# Revit family: BDG_BossDesign_Tbls_ATOM_CircularTables1
name_source: partatom
category: Furniture
revit_build: Autodesk Revit 2016 (Build: 20150714_1515(x64)
units: mm (PartAtom-declared; Revit-internal decimal feet)

## family parameters
Always vertical = Yes
Cut with Voids When Loaded = No
OmniClass Number = 23.40.20.00
OmniClass Title = General Furniture and Specialties
Room Calculation Point = No
Shared = Yes
Work Plane-Based = No

## types (3) — shared parameters
Assembly Code = E2020200
AssetType = Movable
BIMObjectName = BDG_BossDesign_Tables_ATOM_CircularTables
Category = Pr_40_50_21 : Desks, tables and worktops
DurationUnit = year
ExpectedLife = 5
Finish = Black RAL 9005 or White RAL 9016 Painted Leg Finish

Standard Finishes - MFC, MF MDF, Compact Laminate, 
Premium Finishes - Oak & BAW Veneer, Fenix and Linoleum.
FrameMaterial = BDG_Generic_MFC_White
IfcExportAs = IfcFurnishingElementType
IfcExportType = TABLE
Keynote = Pr_40_50_21
ManufacturerURL = www.bossdesign.com
Material = Standard Finishes - MFC, MF MDF, Compact Laminate, 
Premium Finishes - Oak & BAW Veneer, Fenix and Linoleum.
NBSDescription = Tables
NBSReference = 45-35-86/327
Name = Tables_ATOM_CircularTables_BossDesign
NominalHeight = 735 mm
ProductInformation = www.bossdesign.com/product-list/atom-tables
Shape = Circular
TopMaterial = BDG_Generic_Wood_MFC
URL = www.bossdesign.com
Uniclass2015Code = Pr_40_50_21
Uniclass2015Title = Desks, tables and worktops
Uniclass2015Version = Products v1.10
Version = 1
WarrantyDurationLabor = 5
WarrantyDurationParts = 5
WarrantyDurationUnit = year
zero-valued in all types: NumberOfChairs, WorksurfaceArea

## per-type parameters (varying)
| type | FrameLength | Model | ModelNumber | NominalLength | NominalWidth | Size |
| 1200mm Circular Table | 800 mm  [stored 2.62467 ft] | BOSS_ATTC1200 | BOSS_ATTC1200 | 1200 mm | 1200 mm | 1200 x 1200 x 735mm |
| 1500mm Circular Table | 1000 mm  [stored 3.28084 ft] | BOSS_ATTC1500 | BOSS_ATTC1500 | 1500 mm  [stored 4.92126 ft] | 1500 mm  [stored 4.92126 ft] | 1500 x 1500 x 735mm |
| 1000mm Circular Table | 700 mm  [stored 2.29659 ft] | BOSS_ATTC1000 | BOSS_ATTC1000 | 1000 mm  [stored 3.28084 ft] | 1000 mm  [stored 3.28084 ft] | 1000 x 1000 x 735mm |

note: column(s) folded — value = type name in every type: Description, ModelReference

note: [stored X ft] marks values corroborated as IEEE doubles in the binary element streams (Revit-internal decimal feet)

## geometry (parser evidence)
native form markers: Sweep x6
no freeform markers — native parametric forms only
